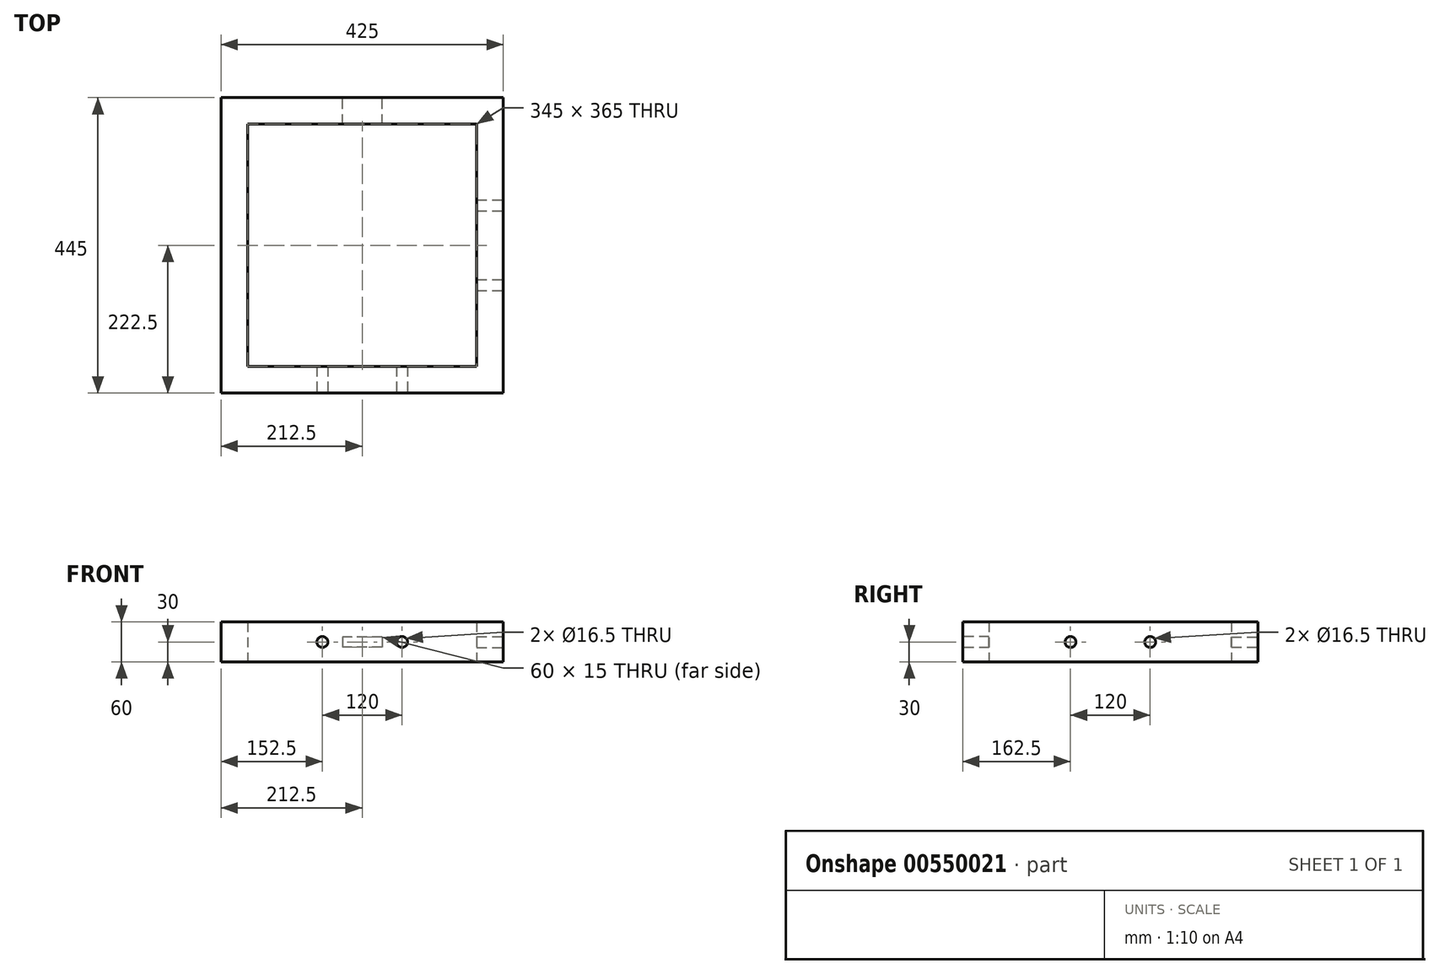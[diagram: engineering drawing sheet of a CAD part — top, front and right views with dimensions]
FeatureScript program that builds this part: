
annotation { "Feature Type Name" : "Feature", "Feature Type Description" : "" }
export const myFeature = defineFeature(function(context is Context, id is Id, definition is map)
    precondition{}
    {
        {
            var Q0;
            Q0=qCreatedBy(makeId("Top.planeOp"),FACE);
            var sketch = newSketch(context, id + "F0", { "sketchPlane" : qUnion([Q0])});
            skLineSegment(sketch, "E0.bottom", {"start": v(212.5, -222.5) * mm, "end": v(-212.5, -222.5) * mm});
            skLineSegment(sketch, "E0.top", {"start": v(212.5, 222.5) * mm, "end": v(-212.5, 222.5) * mm});
            skLineSegment(sketch, "E0.left", {"start": v(212.5, -222.5) * mm, "end": v(212.5, 222.5) * mm});
            skLineSegment(sketch, "E0.right", {"start": v(-212.5, -222.5) * mm, "end": v(-212.5, 222.5) * mm});
            skPoint(sketch, "E0.middle", {"position": v(0, 0) * mm});
            skLineSegment(sketch, "E1.bottom", {"start": v(172.5, -182.5) * mm, "end": v(-172.5, -182.5) * mm});
            skLineSegment(sketch, "E1.top", {"start": v(172.5, 182.5) * mm, "end": v(-172.5, 182.5) * mm});
            skLineSegment(sketch, "E1.left", {"start": v(172.5, -182.5) * mm, "end": v(172.5, 182.5) * mm});
            skLineSegment(sketch, "E1.right", {"start": v(-172.5, -182.5) * mm, "end": v(-172.5, 182.5) * mm});
            skSolve(sketch);
        }
        {
            var Q0;
            Q0 = qSketchRegion(id + "F0", true);
            var Q1;
            Q1 = qConstructionFilter(qBodyType(qCreatedBy(id + "F0" ,EDGE), BodyType.WIRE), ConstructionObject.NO);
            extrude(context, id + "F1", {"entities" : qUnion([Q0]), "surfaceEntities" : qUnion([Q1]), "endBound" : BoundingType.SYMMETRIC, "depth" : 60 * mm, "offsetDistance" : 25 * mm});
        }
        {
            var Q0;
            Q0=makeQuery(id+"F1.opExtrude","SWEPT_FACE",FACE,{"disambiguationData":[OSD([sQuery(id+"F0.wireOp",EDGE,"E0.bottom")])]});
            var sketch = newSketch(context, id + "F2", { "sketchPlane" : qUnion([Q0])});
            skCircle(sketch, "E2", {"center": v(-60, 0) * mm, "radius": 8.25 * mm});
            skCircle(sketch, "E3", {"center": v(60, 0) * mm, "radius": 8.25 * mm});
            skSolve(sketch);
        }
        {
            var Q0;
            Q0 = qSketchRegion(id + "F2", true);
            extrude(context, id + "F3", {"entities" : qUnion([Q0]), "operationType" : NewBodyOperationType.REMOVE, "oppositeDirection" : true, "depth" : 80 * mm, "offsetDistance" : 25 * mm});
        }
        {
            var Q0;
            Q0=makeQuery(id+"F1.opExtrude","SWEPT_FACE",FACE,{"disambiguationData":[OSD([sQuery(id+"F0.wireOp",EDGE,"E0.left")])]});
            var sketch = newSketch(context, id + "F4", { "sketchPlane" : qUnion([Q0])});
            skCircle(sketch, "E4", {"center": v(60, 0) * mm, "radius": 8.25 * mm});
            skCircle(sketch, "E5", {"center": v(-60, 0) * mm, "radius": 8.25 * mm});
            skSolve(sketch);
        }
        {
            var Q0;
            Q0 = qSketchRegion(id + "F4", true);
            extrude(context, id + "F5", {"entities" : qUnion([Q0]), "operationType" : NewBodyOperationType.REMOVE, "oppositeDirection" : true, "depth" : 80 * mm, "offsetDistance" : 25 * mm});
        }
        {
            var Q0;
            Q0=makeQuery(id+"F1.opExtrude","SWEPT_FACE",FACE,{"disambiguationData":[OSD([sQuery(id+"F0.wireOp",EDGE,"E0.top")])]});
            var sketch = newSketch(context, id + "F6", { "sketchPlane" : qUnion([Q0])});
            skLineSegment(sketch, "E6.bottom", {"start": v(-30, 7.5) * mm, "end": v(30, 7.5) * mm});
            skLineSegment(sketch, "E6.top", {"start": v(-30, -7.5) * mm, "end": v(30, -7.5) * mm});
            skLineSegment(sketch, "E6.left", {"start": v(-30, 7.5) * mm, "end": v(-30, -7.5) * mm});
            skLineSegment(sketch, "E6.right", {"start": v(30, 7.5) * mm, "end": v(30, -7.5) * mm});
            skSolve(sketch);
        }
        {
            var Q0;
            Q0 = qSketchRegion(id + "F6", true);
            extrude(context, id + "F7", {"entities" : qUnion([Q0]), "operationType" : NewBodyOperationType.REMOVE, "oppositeDirection" : true, "depth" : 80 * mm, "offsetDistance" : 25 * mm});
        }
    });
